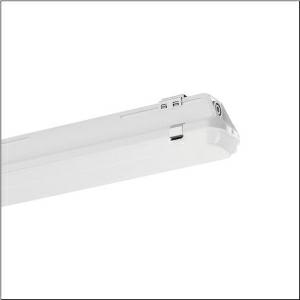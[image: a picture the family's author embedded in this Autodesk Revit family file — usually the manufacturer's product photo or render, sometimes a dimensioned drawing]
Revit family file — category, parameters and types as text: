
# Revit family: monsun_r__11_emergency_51fp107p437l3g_529d
name_source: partatom
category: Lighting Fixtures
units: mm (PartAtom-declared; Revit-internal decimal feet)

## family parameters
Cut with Voids When Loaded = No
Host = Face
Light Source = No
Part Type = Normal
Room Calculation Point = No
Round Connector Dimension = Use Diameter
Shared = No

## types (1)
- --- (1 x LED, 3840 lm, 24.9 W, 4000K)
    Apparent Load = 25 VA
    CIE Flux Codes = 47 77 93 94 100
    Color Rendering = 80
    Color Temperature = 4000K
    Default Elevation = 1800 mm
    Description = Monsun® 11 emergency, damp-proof luminaire, chain hanger, primary optical cover: enclosure, of PMMA, light emission: direct distribution, primary light characteristic: symmetric, installation type: suspended mounting, surface-mounted, horizontal mounting, vertical mounting, LED, rated luminous flux: 3.840lm, luminous efficacy: 182lm/W, light colour: 840, colour temperature: 4000K, control gear: ON/OFF, with terminal, 3-pole, max. 2.5mm², mains connection: 220..240V, AC, 50/60Hz, rated input power: 25W, control gear: single battery element, battery: LiFePO4, 9Ah, luminaire housing, of glass-fibre reinforced polyester, uncoated, bright grey, incl. chain hanger, length: 1.590mm, width: 90mm, height: 88mm, clip for enclosure, of stainless steel (V2A), ceiling mounting element, of stainless steel (V2A), chain hanger, of stainless steel (V2A), protection rating (complete): IP66, insulation class (complete): insulation class I (protective earthing), certification: CE, ENEC, VDE, UKCA, protection symbol: D, impact resistance: IK04, permissible operating ambient temperature: -35..+40°C, standard: EN 50419, EN 60598-2-1, contact your sales advisor before using the luminaires in applications with unclear chemical exposure, large temperature fluctuations or condensation-forming humidity, LABS conformity tested according to VDMA 24364:2018-05, no direct snow, no direct sun, no direct rain, for indoor or canopied outdoor use, corresponds to IFS (International Featured Standards) requirements for safety and quality in the food industry, packaging unit: 1 piece
    Height = 89 mm
    Lamp = 1 x LED
    Lamp Light Flux = 3840 lm
    Lamp Power = 24.9 W
    Lamp count = 1
    Length = 1590 mm
    Luminous efficacy = 154 lm/W
    Manufacturer = Siteco
    ModVariant = No
    Model = 51FP107P437L3G
    Mounting Place = Ceiling
    Mounting Type = Surface mounted
    Number of Poles = 1
    OnlyDefault = Yes
    Power Factor = 1
    Product Name = Monsun® 11 emergency
    Product group = damp-proof luminaire
    ProductGroupID = 301
    Protection Class = Protection class I
    Protection Degree = IP 66
    RLX_Detail_Level = 1
    RLX_Emergency_Light_Flux = 0 lm
    RLX_Emergency_Type = 0
    RLX_Emergency_Type_DB = No
    RlxData = <blob elided: 88661 chars, md5=dc1cbb25>
    Socket = socket
    Standby Power = 0 W
    System Light Flux = 3840 lm
    System Power = 25 W
    Type Comments = : AC-mode
    Type Image = l_1349237.jpg
    URL = http://relux.com
    VarID = @adj_030513
    Voltage = 0 V
    Weight = 0.00 kg
    Width = 90 mm

## geometry (parser evidence)
native form markers: Blend x4, Sweep x12
no freeform markers — native parametric forms only
